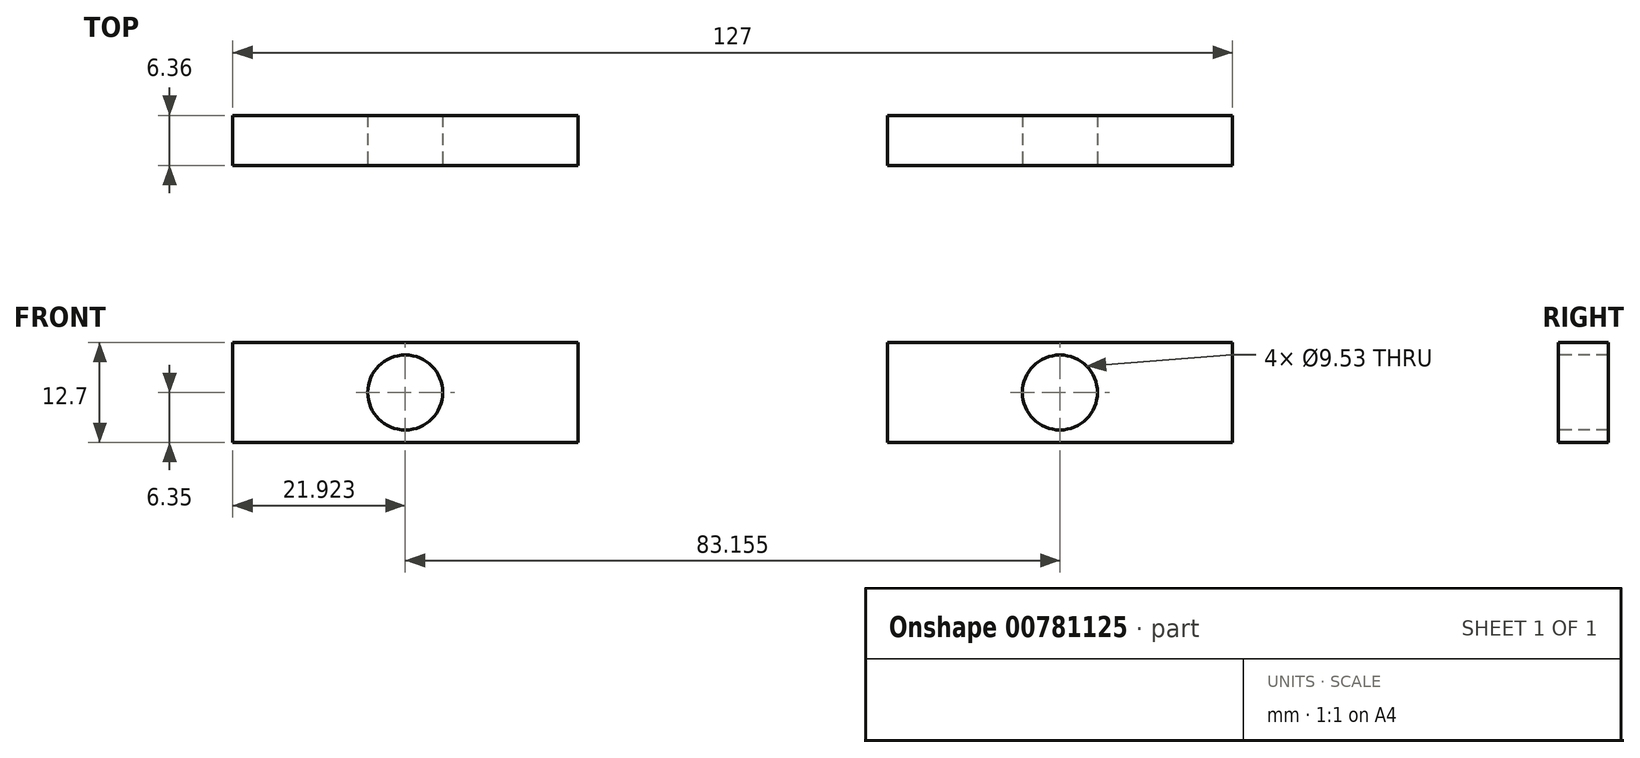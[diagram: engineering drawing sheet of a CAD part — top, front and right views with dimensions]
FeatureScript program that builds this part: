
annotation { "Feature Type Name" : "Feature", "Feature Type Description" : "" }
export const myFeature = defineFeature(function(context is Context, id is Id, definition is map)
    precondition{}
    {
        {
            var Q0;
            Q0=qCreatedBy(makeId("Top.planeOp"),FACE);
            var sketch = newSketch(context, id + "F0", { "sketchPlane" : qUnion([Q0])});
            skLineSegment(sketch, "E0.bottom", {"start": v(63.5, -3.17) * mm, "end": v(19.65, -3.17) * mm});
            skLineSegment(sketch, "E0.top", {"start": v(63.5, 3.18) * mm, "end": v(19.65, 3.18) * mm});
            skLineSegment(sketch, "E0.left", {"start": v(63.5, -3.17) * mm, "end": v(63.5, 3.18) * mm});
            skLineSegment(sketch, "E0.right", {"start": v(-63.5, -3.18) * mm, "end": v(-63.5, 3.17) * mm});
            skPoint(sketch, "E0.middle", {"position": v(0, 0) * mm});
            skPoint(sketch, "E1", {"position": v(-19.65, 3.18) * mm});
            skPoint(sketch, "E2", {"position": v(-19.65, -3.18) * mm});
            skLineSegment(sketch, "E3", {"start": v(-19.65, 3.18) * mm, "end": v(-19.65, -3.18) * mm});
            skPoint(sketch, "E4.MirrorP", {"position": v(19.65, -3.18) * mm});
            skPoint(sketch, "E5.MirrorP", {"position": v(19.65, 3.18) * mm});
            skLineSegment(sketch, "E6", {"start": v(19.65, 3.18) * mm, "end": v(19.65, -3.18) * mm});
            skLineSegment(sketch, "E7.trimOffspring", {"start": v(-19.65, 3.18) * mm, "end": v(-63.5, 3.17) * mm});
            skLineSegment(sketch, "E8.trimOffspring", {"start": v(-19.65, -3.18) * mm, "end": v(-63.5, -3.18) * mm});
            skSolve(sketch);
        }
        {
            var Q0;
            Q0=makeQuery(id+"F0.imprint","IMPRINT",FACE,{"disambiguationData":[TD([[makeQuery(id+"F0.imprint","IMPRINT",EDGE,{"derivedFrom":sQuery(id+"F0.wireOp",EDGE,"E0.right")}),-1.0]])]});
            var Q1;
            Q1=makeQuery(id+"F0.imprint","IMPRINT",FACE,{"disambiguationData":[TD([[makeQuery(id+"F0.imprint","IMPRINT",EDGE,{"derivedFrom":sQuery(id+"F0.wireOp",EDGE,"E0.bottom")}),-1.0]])]});
            extrude(context, id + "F1", {"entities" : qUnion([Q0, Q1]), "depth" : 12.7 * mm, "offsetDistance" : 25.4 * mm});
        }
        {
            var Q0;
            Q0=makeQuery(id+"F1.opExtrude","SWEPT_FACE",FACE,{"disambiguationData":[OSD([sQuery(id+"F0.wireOp",EDGE,"E8.trimOffspring")])]});
            var sketch = newSketch(context, id + "F2", { "sketchPlane" : qUnion([Q0])});
            skCircle(sketch, "E9", {"center": v(-41.58, 6.35) * mm, "radius": 4.76 * mm});
            skCircle(sketch, "E10.MirrorC", {"center": v(41.58, 6.35) * mm, "radius": 4.76 * mm});
            skSolve(sketch);
        }
        {
            var Q0;
            Q0 = qSketchRegion(id + "F2", true);
            extrude(context, id + "F3", {"entities" : qUnion([Q0]), "operationType" : NewBodyOperationType.REMOVE, "oppositeDirection" : true, "depth" : 25.4 * mm, "offsetDistance" : 25.4 * mm});
        }
    });
